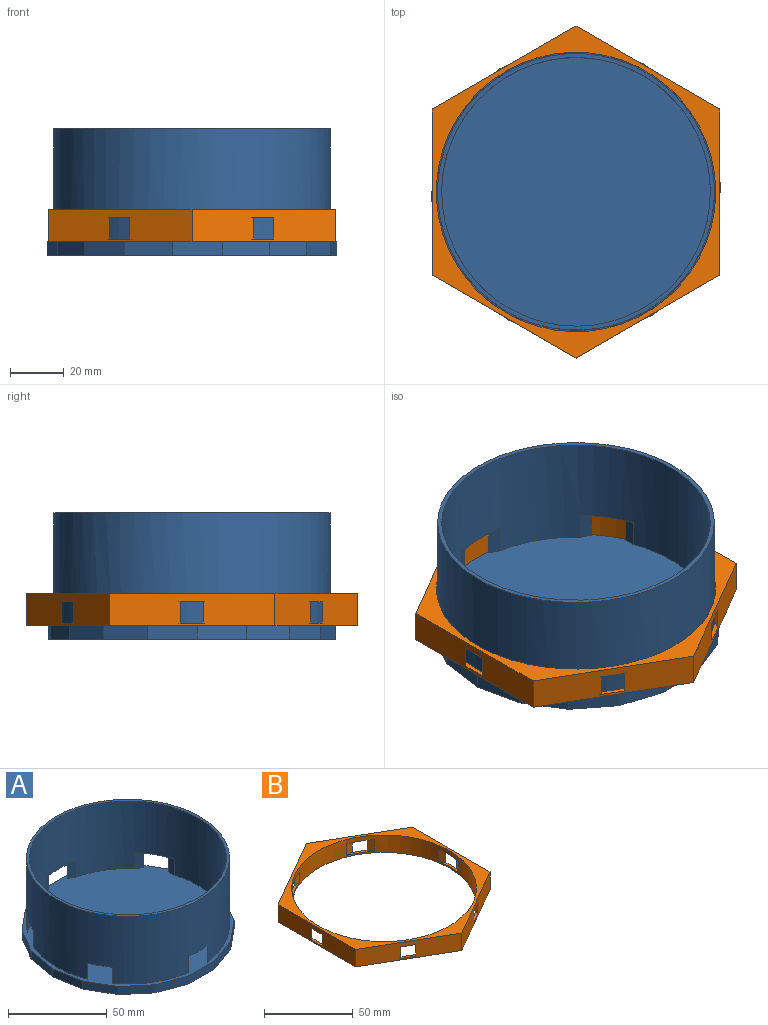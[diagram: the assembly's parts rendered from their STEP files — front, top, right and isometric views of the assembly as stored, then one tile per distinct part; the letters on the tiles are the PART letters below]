
ASSEMBLY  parts=2 mates=1
PART A: 41 faces, bbox 107.9x106.4x47 mm
  f0: cylinder r=50mm len=100mm, axis (0,0,-1), area 11958.5mm2, adj f2,f3,f4,f5,f6,f7,f8,f9
  f1: cylinder r=51.5mm len=103mm, axis (0,0,-1), area 12806.5mm2, adj f2,f3,f4,f5,f6,f7,f8,f9
  f2: plane 103x103mm, normal (0,0,1), area 478.3mm2, adj f0,f1
  f3: plane 17.52x10.57mm, normal (0,0,-1), area 25mm2, adj f0,f1,f4,f5
  f4: plane 10x4.29mm, normal (-1,0.02,0), area 42.9mm2, adj f0,f1,f3,f21
  f5: plane 10x3.75mm, normal (-0.48,0.88,0), area 42.9mm2, adj f0,f1,f3,f21
  f6: plane 20.45x2.76mm, normal (0,0,-1), area 25mm2, adj f0,f1,f7,f8
  f7: plane 10x3.75mm, normal (-0.48,0.88,0), area 42.9mm2, adj f0,f1,f6,f21
  f8: plane 10x3.67mm, normal (0.52,0.86,0), area 42.9mm2, adj f0,f1,f6,f21
  f9: plane 17.91x9.97mm, normal (0,0,-1), area 25mm2, adj f0,f1,f10,f11
  f10: plane 10x3.67mm, normal (0.52,0.86,0), area 42.9mm2, adj f0,f1,f9,f21
  f11: plane 10x4.29mm, normal (1,-0.02,0), area 42.9mm2, adj f0,f1,f9,f21
  f12: plane 17.52x10.57mm, normal (0,0,-1), area 25mm2, adj f0,f1,f13,f14
  f13: plane 10x4.29mm, normal (1,-0.02,0), area 42.9mm2, adj f0,f1,f12,f21
  f14: plane 10x3.75mm, normal (0.48,-0.88,0), area 42.9mm2, adj f0,f1,f12,f21
  f15: plane 20.45x2.76mm, normal (0,0,-1), area 25mm2, adj f0,f1,f16,f17
  f16: plane 10x3.67mm, normal (-0.52,-0.86,0), area 42.9mm2, adj f0,f1,f15,f21
  f17: plane 10x3.75mm, normal (0.48,-0.88,0), area 42.9mm2, adj f0,f1,f15,f21
  f18: plane 17.91x9.97mm, normal (0,0,-1), area 25mm2, adj f0,f1,f19,f20
  f19: plane 10x4.29mm, normal (-1,0.02,0), area 42.9mm2, adj f0,f1,f18,f21
  f20: plane 10x3.67mm, normal (-0.52,-0.86,0), area 42.9mm2, adj f0,f1,f18,f21
  f21: plane 107.95x106.41mm, normal (0,0,1), area 8639.8mm2, adj f0,f1,f4,f5,f7,f8,f10,f11
  f22: plane 16.18x9.46mm, normal (-0.86,0.5,0), area 93.7mm2, adj f21,f23,f39,f40
  f23: plane 18.44x5mm, normal (-0.98,0.18,0), area 93.7mm2, adj f21,f22,f24,f40
  f24: plane 18.48x5mm, normal (-0.99,-0.17,0), area 93.7mm2, adj f21,f23,f25,f40
  f25: plane 16.29x9.28mm, normal (-0.87,-0.5,0), area 93.7mm2, adj f21,f24,f26,f40
  f26: plane 14.29x12.13mm, normal (-0.65,-0.76,0), area 93.7mm2, adj f21,f25,f27,f40
  f27: plane 17.58x6.51mm, normal (-0.35,-0.94,0), area 93.7mm2, adj f21,f26,f28,f40
  f28: plane 18.75x5mm, normal (-0.01,-1,0), area 93.7mm2, adj f21,f27,f29,f40
  f29: plane 17.65x6.31mm, normal (0.34,-0.94,0), area 93.7mm2, adj f21,f28,f30,f40
  f30: plane 14.43x11.97mm, normal (0.64,-0.77,0), area 93.7mm2, adj f21,f29,f31,f40
  f31: plane 16.18x9.46mm, normal (0.86,-0.5,0), area 93.7mm2, adj f21,f30,f32,f40
  f32: plane 18.44x5mm, normal (0.98,-0.18,0), area 93.7mm2, adj f21,f31,f33,f40
  f33: plane 18.48x5mm, normal (0.99,0.17,0), area 93.7mm2, adj f21,f32,f34,f40
  f34: plane 16.29x9.28mm, normal (0.87,0.5,0), area 93.7mm2, adj f21,f33,f35,f40
  f35: plane 14.29x12.13mm, normal (0.65,0.76,0), area 93.7mm2, adj f21,f34,f36,f40
  f36: plane 17.58x6.51mm, normal (0.35,0.94,0), area 93.7mm2, adj f21,f35,f37,f40
  f37: plane 18.75x5mm, normal (0.01,1,0), area 93.7mm2, adj f21,f36,f38,f40
  f38: plane 17.65x6.31mm, normal (-0.34,0.94,0), area 93.7mm2, adj f21,f37,f39,f40
  f39: plane 14.43x11.97mm, normal (-0.64,0.77,0), area 93.7mm2, adj f21,f22,f38,f40
  f40: plane 107.95x106.41mm, normal (0,0,-1), area 8967.8mm2, adj f22,f23,f24,f25,f26,f27,f28,f29
PART B: 33 faces, bbox 107x123.6x12 mm
  f0: plane 53.5x30.89mm, normal (-0.5,-0.87,0), area 672mm2, adj f1,f6,f7,f8,f21,f22,f23,f24
  f1: plane 53.5x30.89mm, normal (0.5,-0.87,0), area 672mm2, adj f0,f2,f7,f8,f17,f18,f19,f20
  f2: plane 61.78x12mm, normal (1,0,0), area 672mm2, adj f1,f3,f7,f8,f13,f14,f15,f16
  f3: plane 53.5x30.89mm, normal (0.5,0.87,0), area 672mm2, adj f2,f4,f7,f8,f29,f30,f31,f32
  f4: plane 53.5x30.89mm, normal (-0.5,0.87,0), area 672mm2, adj f3,f6,f7,f8,f25,f26,f27,f28
  f5: cylinder r=52mm len=104mm, axis (0,0,-1), area 3148.9mm2, adj f7,f8,f9,f10,f11,f12,f13,f14
  f6: plane 61.78x12mm, normal (-1,0,0), area 672mm2, adj f0,f4,f7,f8,f9,f10,f11,f12
  f7: plane 123.55x107mm, normal (0,0,1), area 1420.3mm2, adj f0,f1,f2,f3,f4,f5,f6
  f8: plane 123.55x107mm, normal (0,0,-1), area 1420.3mm2, adj f0,f1,f2,f3,f4,f5,f6
  f9: plane 16.02x2.14mm, normal (0,0,1), area 19.5mm2, adj f5,f6,f11,f12
  f10: plane 16.02x2.14mm, normal (0,0,-1), area 19.5mm2, adj f5,f6,f11,f12
  f11: plane 8x3.66mm, normal (0.87,0.5,0), area 33.8mm2, adj f5,f6,f9,f10
  f12: plane 8x3.68mm, normal (0.86,-0.5,0), area 34.1mm2, adj f5,f6,f9,f10
  f13: plane 16.02x2.14mm, normal (0,0,-1), area 19.5mm2, adj f2,f5,f15,f16
  f14: plane 16.02x2.14mm, normal (0,0,1), area 19.5mm2, adj f2,f5,f15,f16
  f15: plane 8x3.66mm, normal (-0.87,-0.5,0), area 33.8mm2, adj f2,f5,f13,f14
  f16: plane 8x3.68mm, normal (-0.86,0.5,0), area 34.1mm2, adj f2,f5,f13,f14
  f17: plane 13.89x7.99mm, normal (0,0,-1), area 19.5mm2, adj f1,f5,f19,f20
  f18: plane 13.89x7.99mm, normal (0,0,1), area 19.5mm2, adj f1,f5,f19,f20
  f19: plane 8x3.65mm, normal (-0.86,0.5,0), area 33.8mm2, adj f1,f5,f17,f18
  f20: plane 8x4.26mm, normal (0,1,0), area 34.1mm2, adj f1,f5,f17,f18
  f21: plane 13.85x8.04mm, normal (0,0,-1), area 19.5mm2, adj f0,f5,f23,f24
  f22: plane 13.85x8.04mm, normal (0,0,1), area 19.5mm2, adj f0,f5,f23,f24
  f23: plane 8x4.22mm, normal (0,1,0), area 33.8mm2, adj f0,f5,f21,f22
  f24: plane 8x3.69mm, normal (0.87,0.5,0), area 34.1mm2, adj f0,f5,f21,f22
  f25: plane 13.89x7.99mm, normal (0,0,1), area 19.5mm2, adj f4,f5,f27,f28
  f26: plane 13.89x7.99mm, normal (0,0,-1), area 19.5mm2, adj f4,f5,f27,f28
  f27: plane 8x4.26mm, normal (0,-1,0), area 34.1mm2, adj f4,f5,f25,f26
  f28: plane 8x3.65mm, normal (0.86,-0.5,0), area 33.8mm2, adj f4,f5,f25,f26
  f29: plane 8x4.22mm, normal (0,-1,0), area 33.8mm2, adj f3,f5,f30,f31
  f30: plane 13.85x8.04mm, normal (0,0,-1), area 19.5mm2, adj f3,f5,f29,f32
  f31: plane 13.85x8.04mm, normal (0,0,1), area 19.5mm2, adj f3,f5,f29,f32
  f32: plane 8x3.69mm, normal (-0.87,-0.5,0), area 34.1mm2, adj f3,f5,f30,f31
PLACE A rot(axis=(0,0,1),2.5deg) t=(0.56,28.61,11.5)mm
PLACE B t=(0.56,28.61,11.5)mm
MATE revolute A.f1 <-> B.f5  axis (0,0,-1) through (0.56,28.61,32.5)mm
